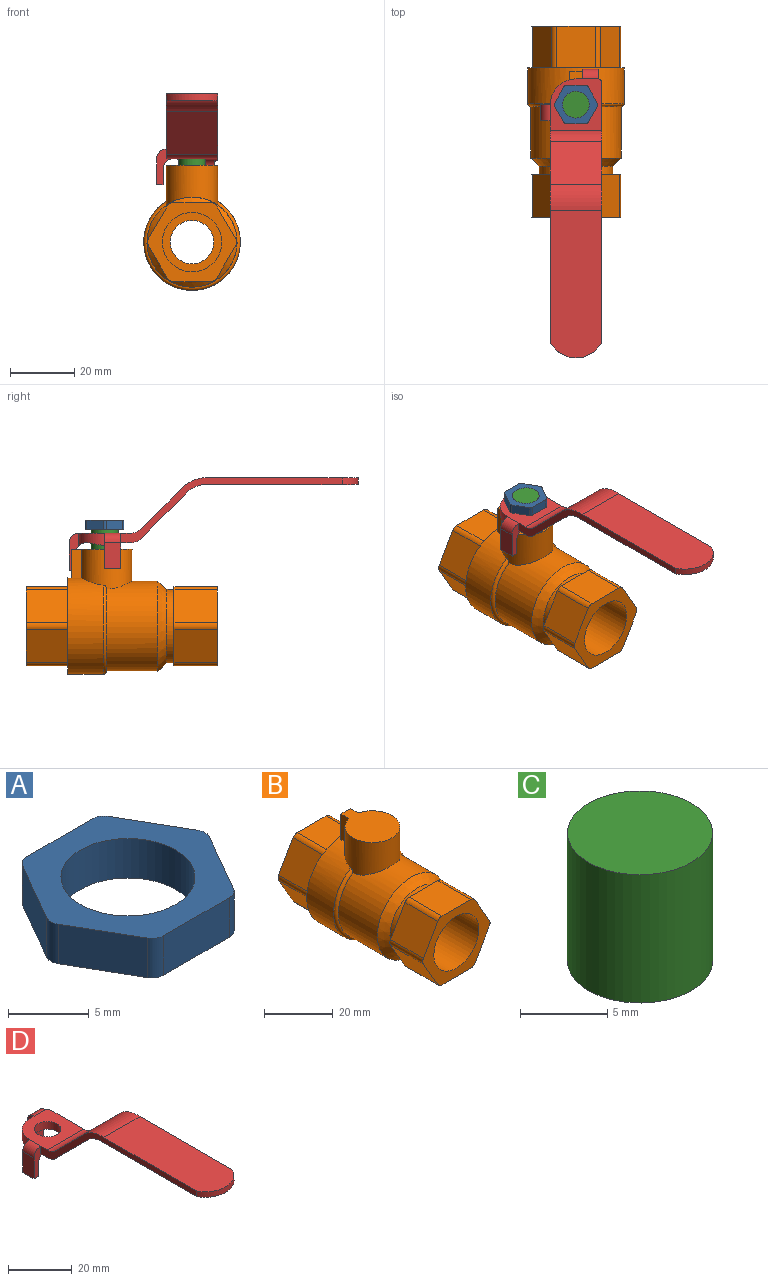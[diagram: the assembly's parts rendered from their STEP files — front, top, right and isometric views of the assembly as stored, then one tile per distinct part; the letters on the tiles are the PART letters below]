
ASSEMBLY  parts=4 mates=3
PART A: 15 faces, bbox 13.5x12x3 mm
  f0: plane 5.77x3mm, normal (0,-1,0), area 17.3mm2, adj f1,f11,f13,f14
  f1: cylinder r=1mm len=3mm, axis (0,0,1), area 3.1mm2, adj f0,f2,f13,f14
  f2: plane 5x3mm, normal (0.87,-0.5,0), area 17.3mm2, adj f1,f3,f13,f14
  f3: cylinder r=1mm len=3mm, axis (0,0,1), area 3.1mm2, adj f2,f4,f13,f14
  f4: plane 5x3mm, normal (0.87,0.5,0), area 17.3mm2, adj f3,f5,f13,f14
  f5: cylinder r=1mm len=3mm, axis (0,0,1), area 3.1mm2, adj f4,f6,f13,f14
  f6: plane 5.77x3mm, normal (0,1,0), area 17.3mm2, adj f5,f7,f13,f14
  f7: cylinder r=1mm len=3mm, axis (0,0,1), area 3.1mm2, adj f6,f8,f13,f14
  f8: plane 5x3mm, normal (-0.87,0.5,0), area 17.3mm2, adj f7,f9,f13,f14
  f9: cylinder r=1mm len=3mm, axis (0,0,1), area 3.1mm2, adj f8,f10,f13,f14
  f10: plane 5x3mm, normal (-0.87,-0.5,0), area 17.3mm2, adj f9,f11,f13,f14
  f11: cylinder r=1mm len=3mm, axis (0,0,1), area 3.1mm2, adj f0,f10,f13,f14
  f12: cylinder r=4.16mm len=8.32mm, axis (0,0,1), area 78.4mm2, adj f13,f14
  f13: plane 13.55x12mm, normal (0,0,1), area 70mm2, adj f0,f1,f2,f3,f4,f5,f6,f7
  f14: plane 13.55x12mm, normal (0,0,-1), area 70mm2, adj f0,f1,f2,f3,f4,f5,f6,f7
PART B: 43 faces, bbox 32.5x59.5x40.1 mm
  f0: cylinder r=14mm len=28mm, axis (0,-1,0), area 1302.3mm2, adj f2,f23,f40
  f1: cylinder r=15mm len=30mm, axis (0,-1,0), area 936.6mm2, adj f2,f4,f38,f39,f40,f41
  f2: torus R=14mm, axis (0,1,0), area 117.9mm2, adj f0,f1,f40
  f3: plane 18.5x18.5mm, normal (0,1,0), area 125.7mm2, adj f21,f35
  f4: plane 30x30mm, normal (0,1,0), area 188.3mm2, adj f1,f24,f25,f26,f27,f28,f29,f30
  f5: plane 13.5x11.84mm, normal (0,0,-1), area 159.8mm2, adj f6,f17,f18,f19
  f6: cylinder r=2mm len=13.5mm, axis (0,1,0), area 28.3mm2, adj f5,f7,f18,f19
  f7: plane 13.5x10.25mm, normal (0.87,0,-0.5), area 159.8mm2, adj f6,f8,f18,f19
  f8: cylinder r=2mm len=13.5mm, axis (0,1,0), area 28.3mm2, adj f7,f9,f18,f19
  f9: plane 13.5x10.25mm, normal (0.87,0,0.5), area 159.8mm2, adj f8,f10,f18,f19
  f10: cylinder r=2mm len=13.5mm, axis (0,1,0), area 28.3mm2, adj f9,f11,f18,f19
  f11: plane 13.5x11.84mm, normal (0,0,1), area 159.8mm2, adj f10,f12,f18,f19
  f12: cylinder r=2mm len=13.5mm, axis (0,1,0), area 28.3mm2, adj f11,f13,f18,f19
  f13: plane 13.5x10.25mm, normal (-0.87,0,0.5), area 159.8mm2, adj f12,f14,f18,f19
  f14: cylinder r=2mm len=13.5mm, axis (0,1,0), area 28.3mm2, adj f13,f15,f18,f19
  f15: plane 13.5x10.25mm, normal (-0.87,0,-0.5), area 159.8mm2, adj f14,f17,f18,f19
  f16: cylinder r=9.25mm len=18.5mm, axis (0,1,0), area 784.6mm2, adj f18,f20
  f17: cylinder r=2mm len=13.5mm, axis (0,1,0), area 28.3mm2, adj f5,f15,f18,f19
  f18: plane 27.67x24.5mm, normal (0,-1,0), area 249.7mm2, adj f5,f6,f7,f8,f9,f10,f11,f12
  f19: plane 27.67x24.5mm, normal (0,1,0), area 110.2mm2, adj f5,f6,f7,f8,f9,f10,f11,f12
  f20: plane 18.5x18.5mm, normal (0,-1,0), area 125.7mm2, adj f16,f21
  f21: cylinder r=6.75mm len=33mm, axis (0,-1,0), area 1399.6mm2, adj f3,f20
  f22: cylinder r=11.4mm len=22.8mm, axis (0,-1,0), area 172mm2, adj f19,f23
  f23: cone r=14mm half-angle=45deg, axis (0,1,0), area 293.4mm2, adj f0,f22
  f24: plane 13x11.84mm, normal (0,0,-1), area 153.9mm2, adj f4,f25,f36,f37
  f25: cylinder r=2mm len=13mm, axis (0,-1,0), area 27.2mm2, adj f4,f24,f26,f37
  f26: plane 13x10.25mm, normal (-0.87,0,-0.5), area 153.9mm2, adj f4,f25,f27,f37
  f27: cylinder r=2mm len=13mm, axis (0,-1,0), area 27.2mm2, adj f4,f26,f28,f37
  f28: plane 13x10.25mm, normal (-0.87,0,0.5), area 153.9mm2, adj f4,f27,f29,f37
  f29: cylinder r=2mm len=13mm, axis (0,-1,0), area 27.2mm2, adj f4,f28,f30,f37
  f30: plane 13x11.84mm, normal (0,0,1), area 153.9mm2, adj f4,f29,f31,f37
  f31: cylinder r=2mm len=13mm, axis (0,-1,0), area 27.2mm2, adj f4,f30,f32,f37
  f32: plane 13x10.25mm, normal (0.87,0,0.5), area 153.9mm2, adj f4,f31,f33,f37
  f33: cylinder r=2mm len=13mm, axis (0,-1,0), area 27.2mm2, adj f4,f32,f34,f37
  f34: plane 13x10.25mm, normal (0.87,0,-0.5), area 153.9mm2, adj f4,f33,f36,f37
  f35: cylinder r=9.25mm len=18.5mm, axis (0,-1,0), area 755.6mm2, adj f3,f37
  f36: cylinder r=2mm len=13mm, axis (0,-1,0), area 27.2mm2, adj f4,f24,f34,f37
  f37: plane 27.67x24.5mm, normal (0,1,0), area 249.7mm2, adj f24,f25,f26,f27,f28,f29,f30,f31
  f38: plane 9.03x3.25mm, normal (1,0,0), area 29.4mm2, adj f1,f40,f41,f42
  f39: plane 9.03x3.25mm, normal (-1,0,0), area 29.4mm2, adj f1,f40,f41,f42
  f40: cylinder r=8mm len=16mm, axis (0,0,-1), area 495.8mm2, adj f0,f1,f2,f38,f39,f42
  f41: plane 9.03x4mm, normal (0,1,0), area 35.8mm2, adj f1,f38,f39,f42
  f42: plane 19x16mm, normal (0,0,1), area 213.4mm2, adj f38,f39,f40,f41
PART C: 3 faces, bbox 8.3x8.3x9 mm
  f0: cylinder r=4.16mm len=9mm, axis (0,0,-1), area 235.3mm2, adj f1,f2
  f1: plane 8.32x8.32mm, normal (0,0,1), area 54.4mm2, adj f0
  f2: plane 8.32x8.32mm, normal (0,0,-1), area 54.4mm2, adj f0
PART D: 33 faces, bbox 19x89.7x28.8 mm
  f0: plane 16x13.93mm, normal (0,0,-1), area 146.2mm2, adj f4,f5,f7,f8,f16,f24,f29,f31
  f1: plane 11.56x0.02mm, normal (0,-0.71,-0.71), area 0.3mm2, adj f3,f17,f18
  f2: plane 45.86x16mm, normal (0,0,1), area 711.2mm2, adj f4,f7,f13,f17
  f3: plane 45.86x16mm, normal (0,0,-1), area 728.3mm2, adj f1,f4,f7,f14,f17
  f4: plane 68.78x20.29mm, normal (-1,0,0), area 164.9mm2, adj f0,f2,f3,f9,f11,f12,f13,f14
  f5: cylinder r=8mm len=8mm, axis (0,0,1), area 42.1mm2, adj f0,f6,f9,f25,f29,f31
  f6: plane 3.76x2mm, normal (0,1,0), area 7.5mm2, adj f5,f9,f19,f31
  f7: plane 80.78x20.46mm, normal (1,0,0), area 201mm2, adj f0,f2,f3,f9,f10,f11,f12,f13
  f8: cylinder r=4.16mm len=8.32mm, axis (0,0,1), area 78.4mm2, adj f0,f9
  f9: plane 16x15.93mm, normal (0,0,1), area 186.5mm2, adj f4,f5,f6,f7,f8,f10,f15,f30
  f10: cylinder r=1mm len=3.76mm, axis (0,0,-1), area 5.4mm2, adj f7,f9,f20,f31
  f11: plane 16x13.28mm, normal (0,0.71,0.71), area 300.6mm2, adj f4,f7,f13,f15
  f12: plane 16x13.28mm, normal (0,-0.71,-0.71), area 300.6mm2, adj f4,f7,f14,f16
  f13: cylinder r=11.11mm len=16mm, axis (1,0,0), area 139.6mm2, adj f2,f4,f7,f11
  f14: cylinder r=9mm len=16mm, axis (1,0,0), area 113.1mm2, adj f3,f4,f7,f12
  f15: cylinder r=5mm len=16mm, axis (-1,0,0), area 62.8mm2, adj f4,f7,f9,f11
  f16: cylinder r=5mm len=16mm, axis (-1,0,0), area 62.8mm2, adj f0,f4,f7,f12
  f17: cylinder r=8.94mm len=16mm, axis (0,0,1), area 41.8mm2, adj f1,f2,f3,f4,f7,f18
  f18: plane 11.51x2.1mm, normal (0,0,-1), area 16.5mm2, adj f1,f17
  f19: plane 11.5x3mm, normal (-1,0,0), area 25.5mm2, adj f6,f21,f22,f23,f31,f32
  f20: plane 11.5x3mm, normal (1,0,0), area 25.5mm2, adj f10,f21,f22,f23,f31,f32
  f21: plane 8.5x5mm, normal (0,1,0), area 42.5mm2, adj f19,f20,f23,f32
  f22: plane 5.5x5mm, normal (0,-1,0), area 27.5mm2, adj f19,f20,f23,f31
  f23: plane 5x2mm, normal (0,0,-1), area 10mm2, adj f19,f20,f21,f22
  f24: plane 11x5mm, normal (0,-1,0), area 25mm2, adj f0,f4,f26,f27,f28,f29,f30
  f25: plane 11x3mm, normal (0,1,0), area 24.5mm2, adj f5,f26,f27,f28,f29,f30
  f26: plane 8x5mm, normal (-1,0,0), area 40mm2, adj f24,f25,f28,f30
  f27: plane 5x5mm, normal (1,0,0), area 25mm2, adj f24,f25,f28,f29
  f28: plane 5x2mm, normal (0,0,-1), area 10mm2, adj f24,f25,f26,f27
  f29: cylinder r=3mm len=10.29mm, axis (0,-1,0), area 31.3mm2, adj f0,f5,f24,f25,f27
  f30: cylinder r=3mm len=5mm, axis (0,-1,0), area 23.6mm2, adj f9,f24,f25,f26
  f31: cylinder r=3mm len=13.29mm, axis (-1,0,0), area 37.6mm2, adj f0,f5,f6,f7,f10,f19,f20,f22
  f32: cylinder r=3mm len=5mm, axis (-1,0,0), area 23.6mm2, adj f9,f19,f20,f21
PLACE A t=(0,0.55,0)mm
PLACE B at identity
PLACE C rot(axis=(1,0,0),180deg) t=(0,42.55,56.79)mm
PLACE D t=(0,0.55,0)mm
MATE fastened C.f0 <-> B.f42  axis (0,0,-1) through (0,21.55,23.89)mm
MATE fastened A.f12 <-> C.f0  axis (0,0,1) through (0,21.55,32.89)mm
MATE fastened D.f5 <-> A.f12  axis (0,0,1) through (0,21.55,28.89)mm
